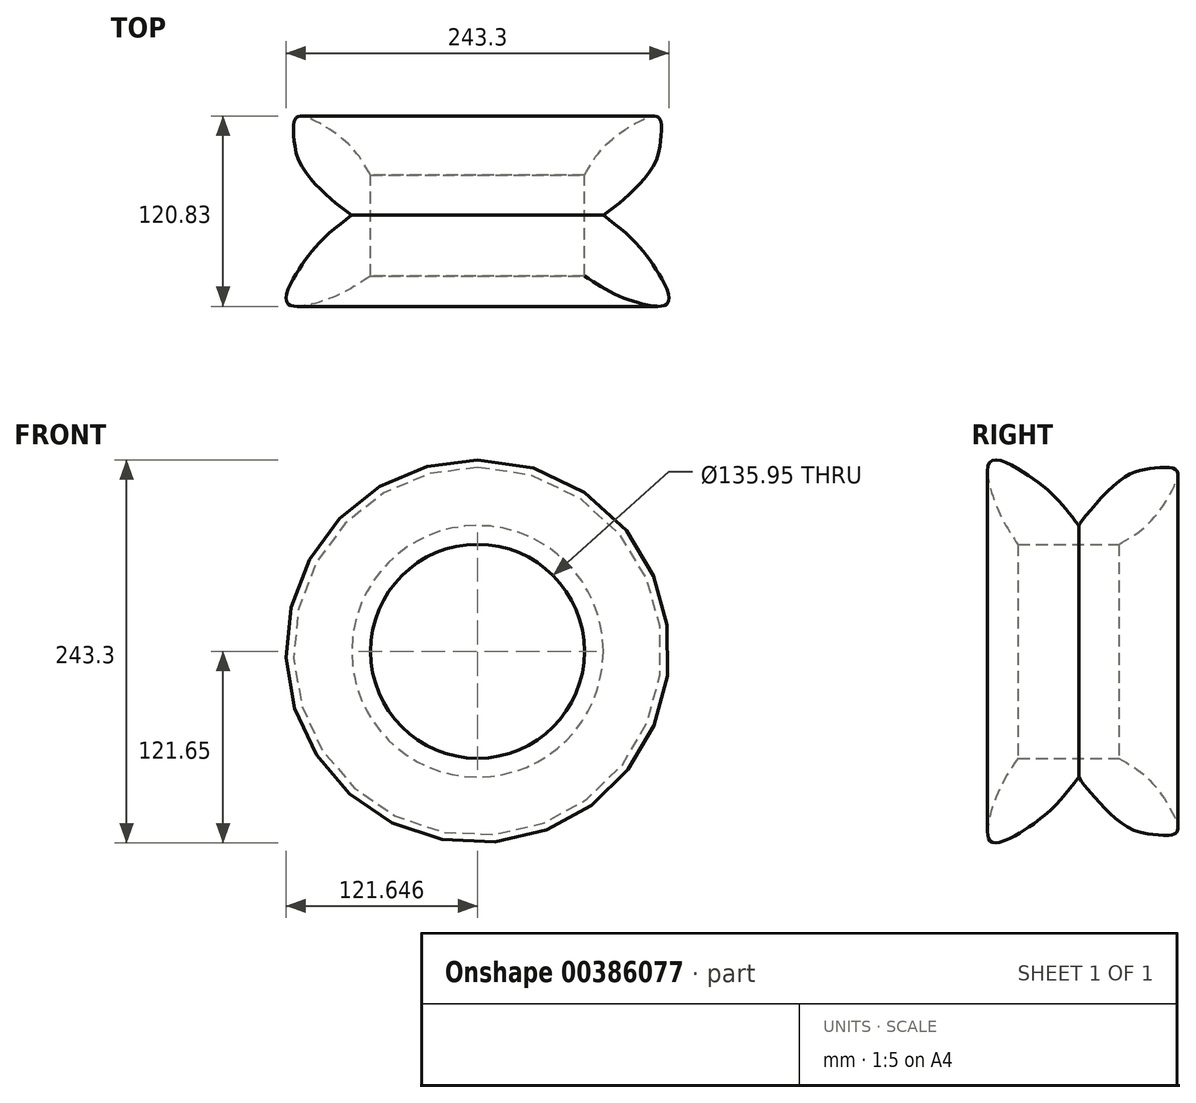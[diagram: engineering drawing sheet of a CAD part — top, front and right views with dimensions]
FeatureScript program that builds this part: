
annotation { "Feature Type Name" : "Feature", "Feature Type Description" : "" }
export const myFeature = defineFeature(function(context is Context, id is Id, definition is map)
    precondition{}
    {
        {
            var Q0;
            Q0=qCreatedBy(makeId("Top.planeOp"),FACE);
            var sketch = newSketch(context, id + "F0", { "sketchPlane" : qUnion([Q0])});
            skFitSpline(sketch, "E0", {"points": [v(0, 30.33) * mm, v(13.41, 49.54) * mm, v(37.8, 66) * mm, v(47.25, 66.92) * mm, v(48.47, 52.9) * mm, v(39.63, 30.03) * mm, v(11.9, 5.03) * mm, v(11.59, 5.03) * mm], "startDerivative": vector(64.75, 116.4) * mm, "endDerivative": vector(-9.42, 5.43) * mm});
            skFitSpline(sketch, "E1", {"points": [v(11.9, 5.03) * mm, v(29.27, -9.29) * mm, v(46.03, -30.32) * mm, v(52.74, -51.05) * mm, v(25.91, -48) * mm, v(0, -33.68) * mm], "startDerivative": vector(95, -72.22) * mm, "endDerivative": vector(-105.42, 70.79) * mm});
            skLineSegment(sketch, "E2", {"start": v(0, 30.33) * mm, "end": v(0, -33.68) * mm});
            skLineSegment(sketch, "E3", {"start": v(-67.97, 51.05) * mm, "end": v(-67.97, -70.27) * mm});
            skSolve(sketch);
        }
        {
            var Q0;
            {var subQ2=sQuery(id+"F0.wireOp",EDGE,"E1");Q0=makeQuery(id+"F0.imprint","IMPRINT",FACE,{"disambiguationData":[TD([[makeQuery(id+"F0.imprint","IMPRINT",EDGE,{"derivedFrom":subQ2}),-1.0]])]});}
            var Q1;
            Q1=sQuery(id+"F0.wireOp",EDGE,"E3");
            revolve(context, id + "F1", {"entities" : qUnion([Q0]), "axis" : qUnion([Q1]), "revolveType" : RevolveType.FULL});
        }
    });
